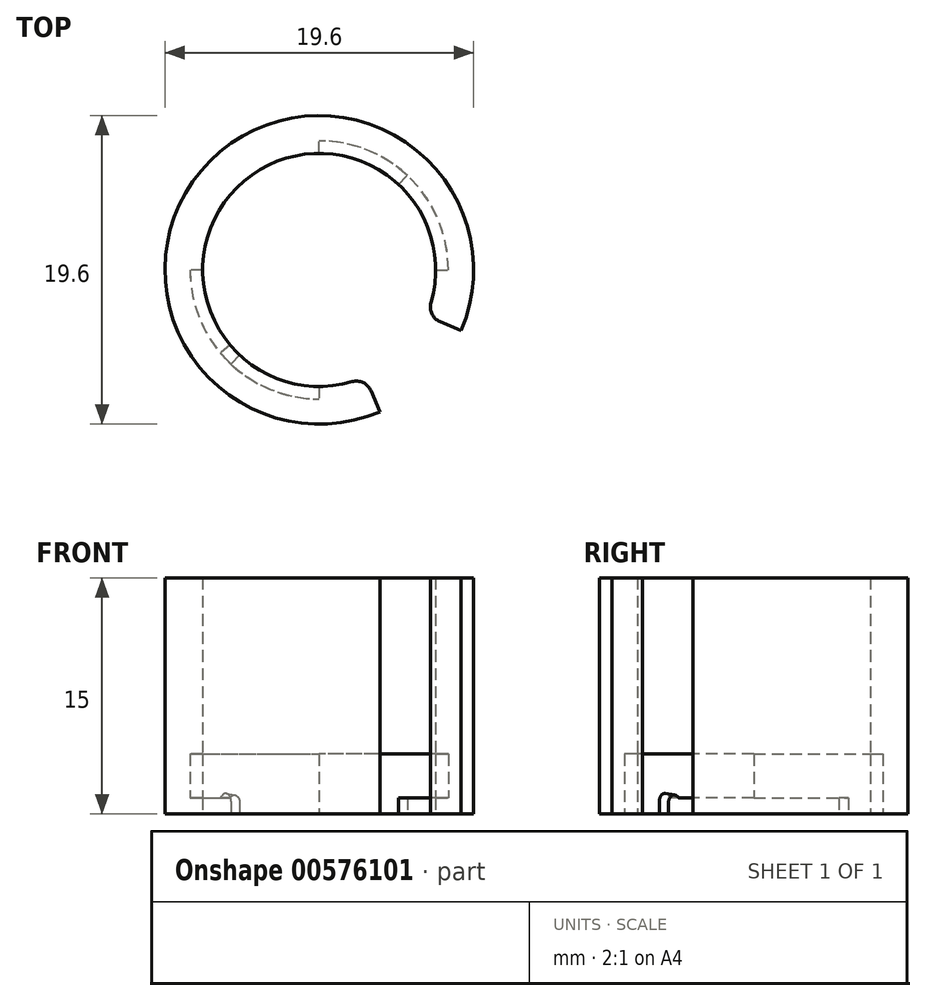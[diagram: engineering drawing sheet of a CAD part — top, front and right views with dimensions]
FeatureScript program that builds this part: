
annotation { "Feature Type Name" : "Feature", "Feature Type Description" : "" }
export const myFeature = defineFeature(function(context is Context, id is Id, definition is map)
    precondition{}
    {
        {
            var Q0;
            Q0=qCreatedBy(makeId("Top.planeOp"),FACE);
            var sketch = newSketch(context, id + "F0", { "sketchPlane" : qUnion([Q0])});
            skCircle(sketch, "E0", {"center": v(0, 0) * mm, "radius": 7.4 * mm});
            skCircle(sketch, "E1", {"center": v(0, 0) * mm, "radius": 9.8 * mm});
            skSolve(sketch);
        }
        {
            var Q0;
            Q0 = qSketchRegion(id + "F0", true);
            extrude(context, id + "F1", {"entities" : qUnion([Q0]), "depth" : 10 * mm, "offsetDistance" : 25 * mm});
        }
        {
            var Q0;
            Q0=qCreatedBy(makeId("Top.planeOp"),FACE);
            cPlane(context, id + "F2", {"entities" : qUnion([Q0]), "cplaneType" : CPlaneType.OFFSET, "offset" : 1 * mm, "width" : 150 * mm, "height" : 150 * mm});
        }
        {
            var Q0;
            Q0=qCreatedBy(id+"F2.planeOp",FACE);
            var sketch = newSketch(context, id + "F3", { "sketchPlane" : qUnion([Q0])});
            skCircle(sketch, "E2.0", {"center": v(0, 0) * mm, "radius": 7.4 * mm});
            skArc(sketch, "E3", {"start": v(-8.2, 0) * mm, "mid": v(-5.8, -5.8) * mm, "end": v(0, -8.2) * mm});
            skLineSegment(sketch, "E4", {"start": v(0, 0) * mm, "end": v(-8.2, 0) * mm});
            skLineSegment(sketch, "E5", {"start": v(0, 0) * mm, "end": v(0, -8.2) * mm});
            skLineSegment(sketch, "E6", {"start": v(0, 0) * mm, "end": v(0, 8.2) * mm});
            skLineSegment(sketch, "E7", {"start": v(0, 0) * mm, "end": v(8.2, 0) * mm});
            skArc(sketch, "E8.trimOffspring", {"start": v(8.2, 0) * mm, "mid": v(5.8, 5.8) * mm, "end": v(0, 8.2) * mm});
            skSolve(sketch);
        }
        {
            var Q0;
            {var subQ5=sQuery(id+"F3.wireOp",EDGE,"E8.trimOffspring");Q0=makeQuery(id+"F3.imprint","IMPRINT",FACE,{"disambiguationData":[TD([[makeQuery(id+"F3.imprint","IMPRINT",EDGE,{"derivedFrom":subQ5}),1.0]])]});}
            var Q1;
            {var subQ5=sQuery(id+"F3.wireOp",EDGE,"E3");Q1=makeQuery(id+"F3.imprint","IMPRINT",FACE,{"disambiguationData":[TD([[makeQuery(id+"F3.imprint","IMPRINT",EDGE,{"derivedFrom":subQ5}),1.0]])]});}
            extrude(context, id + "F4", {"entities" : qUnion([Q0, Q1]), "operationType" : NewBodyOperationType.REMOVE, "depth" : 2.8 * mm, "offsetDistance" : 25 * mm});
        }
        {
            var Q0;
            Q0=makeQuery(id+"F4.boolean.opBoolean","COPY",FACE,{"derivedFrom":makeQuery(id+"F4.opExtrude","CAP_FACE",FACE,{"disambiguationData":[OSD([sQuery(id+"F3.wireOp",EDGE,"E2.0"),sQuery(id+"F3.wireOp",EDGE,"E3"),sQuery(id+"F3.wireOp",EDGE,"E4"),sQuery(id+"F3.wireOp",EDGE,"E5")])],"isStart":true})});
            var sketch = newSketch(context, id + "F5", { "sketchPlane" : qUnion([Q0])});
            skArc(sketch, "E9.0.0", {"start": v(0, -7.4) * mm, "mid": v(-5.23, -5.23) * mm, "end": v(-7.4, 0) * mm});
            skLineSegment(sketch, "E9.0.1", {"start": v(-7.4, 0) * mm, "end": v(-8.2, 0) * mm});
            skArc(sketch, "E9.0.2", {"start": v(-8.2, 0) * mm, "mid": v(-5.8, -5.8) * mm, "end": v(0, -8.2) * mm});
            skLineSegment(sketch, "E9.0.3", {"start": v(0, -8.2) * mm, "end": v(0, -7.4) * mm});
            skArc(sketch, "E10.0.0", {"start": v(0, 7.4) * mm, "mid": v(5.23, 5.23) * mm, "end": v(7.4, 0) * mm});
            skLineSegment(sketch, "E10.0.1", {"start": v(7.4, 0) * mm, "end": v(8.2, 0) * mm});
            skArc(sketch, "E10.0.2", {"start": v(8.2, 0) * mm, "mid": v(5.8, 5.8) * mm, "end": v(0, 8.2) * mm});
            skLineSegment(sketch, "E10.0.3", {"start": v(0, 8.2) * mm, "end": v(0, 7.4) * mm});
            skLineSegment(sketch, "E11", {"start": v(0, 0) * mm, "end": v(5.05, 6.46) * mm});
            skLineSegment(sketch, "E12", {"start": v(0, 0) * mm, "end": v(-5.05, -6.46) * mm});
            skLineSegment(sketch, "E13", {"start": v(0, 0) * mm, "end": v(-6.28, -5.27) * mm});
            skLineSegment(sketch, "E14", {"start": v(0, 0) * mm, "end": v(6.28, 5.27) * mm});
            skSolve(sketch);
        }
        {
            var Q0;
            {var subQ0=sQuery(id+"F5.wireOp",EDGE,"E13");var subQ1=sQuery(id+"F5.wireOp",EDGE,"E9.0.0");var subQ2=makeQuery(id+"F5.imprint","INTERSECT",VERTEX,{"derivedFrom":[subQ1,subQ0]});Q0=makeQuery(id+"F5.imprint","IMPRINT",FACE,{"disambiguationData":[TD([[makeQuery(id+"F5.imprint","IMPRINT",EDGE,{"disambiguationData":[TD([[subQ2,-1.0]])],"derivedFrom":subQ1}),-1.0]])]});}
            var Q1;
            {var subQ0=sQuery(id+"F5.wireOp",EDGE,"E11");var subQ1=sQuery(id+"F5.wireOp",EDGE,"E10.0.0");var subQ2=makeQuery(id+"F5.imprint","INTERSECT",VERTEX,{"derivedFrom":[subQ1,subQ0]});Q1=makeQuery(id+"F5.imprint","IMPRINT",FACE,{"disambiguationData":[TD([[makeQuery(id+"F5.imprint","IMPRINT",EDGE,{"disambiguationData":[TD([[subQ2,-1.0]])],"derivedFrom":subQ1}),1.0]])]});}
            extrude(context, id + "F6", {"entities" : qUnion([Q0, Q1]), "operationType" : NewBodyOperationType.ADD, "depth" : 1 * mm, "offsetDistance" : 25 * mm});
        }
        {
            var Q0;
            Q0=makeQuery(id+"F6.opExtrude","CAP_EDGE",EDGE,{"disambiguationData":[OSD([sQuery(id+"F5.wireOp",EDGE,"E14")])],"isStart":false});
            var Q1;
            Q1=makeQuery(id+"F6.opExtrude","CAP_EDGE",EDGE,{"disambiguationData":[OSD([sQuery(id+"F5.wireOp",EDGE,"E13")])],"isStart":false});
            chamfer(context, id + "F7", {"entities" : qUnion([Q0, Q1]), "width" : 1 * mm, "tangentPropagation" : true});
        }
        {
            var Q0;
            Q0=makeQuery(id+"F6.opExtrude","CAP_EDGE",EDGE,{"disambiguationData":[OSD([sQuery(id+"F5.wireOp",EDGE,"E12")])],"isStart":false});
            var Q1;
            Q1=makeQuery(id+"F6.opExtrude","CAP_EDGE",EDGE,{"disambiguationData":[OSD([sQuery(id+"F5.wireOp",EDGE,"E11")])],"isStart":false});
            fillet(context, id + "F8", {"entities" : qUnion([Q0, Q1]), "radius" : 0.5 * mm, "tangentPropagation" : true, "allowEdgeOverflow" : false});
        }
        {
            var Q0;
            Q0=makeQuery(id+"F1.opExtrude","CAP_FACE",FACE,{"disambiguationData":[OSD([sQuery(id+"F0.wireOp",EDGE,"E0"),sQuery(id+"F0.wireOp",EDGE,"E1")])],"isStart":true});
            var sketch = newSketch(context, id + "F9", { "sketchPlane" : qUnion([Q0])});
            skArc(sketch, "E15.0.0", {"start": v(7.4, 0) * mm, "mid": v(5.23, -5.23) * mm, "end": v(0, -7.4) * mm});
            skLineSegment(sketch, "E15.0.1", {"start": v(0, -7.4) * mm, "end": v(0, -8.2) * mm});
            skArc(sketch, "E15.0.2", {"start": v(0, -8.2) * mm, "mid": v(5.8, -5.8) * mm, "end": v(8.2, 0) * mm});
            skLineSegment(sketch, "E15.0.3", {"start": v(8.2, 0) * mm, "end": v(7.4, 0) * mm});
            skArc(sketch, "E16.0.0", {"start": v(-7.4, 0) * mm, "mid": v(-5.23, 5.23) * mm, "end": v(0, 7.4) * mm});
            skLineSegment(sketch, "E16.0.1", {"start": v(0, 7.4) * mm, "end": v(0, 8.2) * mm});
            skArc(sketch, "E16.0.2", {"start": v(0, 8.2) * mm, "mid": v(-5.8, 5.8) * mm, "end": v(-8.2, 0) * mm});
            skLineSegment(sketch, "E16.0.3", {"start": v(-8.2, 0) * mm, "end": v(-7.4, 0) * mm});
            skLineSegment(sketch, "E17", {"start": v(-5.05, 5.41) * mm, "end": v(-5.6, 6) * mm});
            skLineSegment(sketch, "E18", {"start": v(5.05, -5.41) * mm, "end": v(5.6, -6) * mm});
            skSolve(sketch);
        }
        {
            var Q0;
            {var subQ0=sQuery(id+"F9.wireOp",EDGE,"E15.0.1");Q0=makeQuery(id+"F9.imprint","IMPRINT",FACE,{"disambiguationData":[TD([[makeQuery(id+"F9.imprint","IMPRINT",EDGE,{"derivedFrom":subQ0}),1.0]])]});}
            var Q1;
            {var subQ0=sQuery(id+"F9.wireOp",EDGE,"E16.0.1");Q1=makeQuery(id+"F9.imprint","IMPRINT",FACE,{"disambiguationData":[TD([[makeQuery(id+"F9.imprint","IMPRINT",EDGE,{"derivedFrom":subQ0}),1.0]])]});}
            var Q2;
            {var subQ0=sQuery(id+"F3.wireOp",EDGE,"E8.trimOffspring");var subQ1=sQuery(id+"F3.wireOp",EDGE,"E6");Q2=makeQuery(id+"F6.boolean.opBoolean","SPLIT",FACE,{"disambiguationData":[TD([makeQuery(id+"F4.boolean.opBoolean","COPY",FACE,{"derivedFrom":makeQuery(id+"F4.opExtrude","SWEPT_FACE",FACE,{"disambiguationData":[OSD([subQ1])]})})])],"derivedFrom":makeQuery(id+"F4.boolean.opBoolean","COPY",FACE,{"derivedFrom":makeQuery(id+"F4.opExtrude","CAP_FACE",FACE,{"disambiguationData":[OSD([sQuery(id+"F3.wireOp",EDGE,"E2.0"),subQ1,sQuery(id+"F3.wireOp",EDGE,"E7"),subQ0])],"isStart":true})})});}
            extrude(context, id + "F10", {"entities" : qUnion([Q0, Q1]), "operationType" : NewBodyOperationType.REMOVE, "oppositeDirection" : true, "depth" : 3 * mm, "endBoundEntityFace" : qUnion([Q2]), "offsetDistance" : 25 * mm});
        }
        {
            var Q0;
            Q0=makeQuery(id+"F10.boolean.opBoolean","INTERSECT",EDGE,{"derivedFrom":[makeQuery(id+"F7.opChamfer","BLEND_FACE",FACE,{"disambiguationData":[OSD([sQuery(id+"F5.wireOp",EDGE,"E14")])]}),makeQuery(id+"F10.opExtrude","SWEPT_FACE",FACE,{"disambiguationData":[OSD([sQuery(id+"F9.wireOp",EDGE,"E18")])]})]});
            var Q1;
            Q1=makeQuery(id+"F10.boolean.opBoolean","INTERSECT",EDGE,{"derivedFrom":[makeQuery(id+"F7.opChamfer","BLEND_FACE",FACE,{"disambiguationData":[OSD([sQuery(id+"F5.wireOp",EDGE,"E13")])]}),makeQuery(id+"F10.opExtrude","SWEPT_FACE",FACE,{"disambiguationData":[OSD([sQuery(id+"F9.wireOp",EDGE,"E17")])]})]});
            fillet(context, id + "F11", {"entities" : qUnion([Q0, Q1]), "radius" : 0.5 * mm, "tangentPropagation" : true, "allowEdgeOverflow" : false});
        }
        {
            var Q0;
            Q0=makeQuery(id+"F1.opExtrude","CAP_FACE",FACE,{"disambiguationData":[OSD([sQuery(id+"F0.wireOp",EDGE,"E0"),sQuery(id+"F0.wireOp",EDGE,"E1")])],"isStart":true});
            var sketch = newSketch(context, id + "F12", { "sketchPlane" : qUnion([Q0])});
            skCircle(sketch, "E19.0.0", {"center": v(0, 0) * mm, "radius": 9.8 * mm});
            skSolve(sketch);
        }
        {
            var Q0;
            Q0=makeQuery(id+"F1.opExtrude","CAP_FACE",FACE,{"disambiguationData":[OSD([sQuery(id+"F0.wireOp",EDGE,"E0"),sQuery(id+"F0.wireOp",EDGE,"E1")])],"isStart":false});
            extrude(context, id + "F13", {"entities" : qUnion([Q0]), "operationType" : NewBodyOperationType.ADD, "depth" : 5 * mm, "offsetDistance" : 25 * mm});
        }
        {
            var Q0;
            Q0=makeQuery(id+"F13.opExtrude","CAP_FACE",FACE,{"disambiguationData":[OSD([sQuery(id+"F0.wireOp",EDGE,"E0"),sQuery(id+"F0.wireOp",EDGE,"E1")])],"isStart":false});
            var sketch = newSketch(context, id + "F14", { "sketchPlane" : qUnion([Q0])});
            skCircle(sketch, "E20.0.0", {"center": v(0, 0) * mm, "radius": 9.8 * mm});
            skCircle(sketch, "E21.0", {"center": v(0, 0) * mm, "radius": 7.4 * mm});
            skLineSegment(sketch, "E22", {"start": v(0, 0) * mm, "end": v(8.18, -8.18) * mm, "construction": true});
            skLineSegment(sketch, "E23", {"start": v(0, 0) * mm, "end": v(4.47, -10.43) * mm});
            skLineSegment(sketch, "E24", {"start": v(0, 0) * mm, "end": v(9.6, -4.12) * mm});
            skLineSegment(sketch, "E25", {"start": v(6.8, -2.91) * mm, "end": v(2.91, -6.8) * mm, "construction": true});
            skArc(sketch, "E26", {"start": v(4.47, -10.43) * mm, "mid": v(8.29, -8.29) * mm, "end": v(9.6, -4.12) * mm});
            skSolve(sketch);
        }
        {
            var Q0;
            {var subQ5=sQuery(id+"F14.wireOp",EDGE,"E26");Q0=makeQuery(id+"F14.imprint","IMPRINT",FACE,{"disambiguationData":[TD([[makeQuery(id+"F14.imprint","IMPRINT",EDGE,{"derivedFrom":subQ5}),1.0]])]});}
            var Q1;
            {var subQ0=sQuery(id+"F14.wireOp",EDGE,"E23");var subQ1=sQuery(id+"F14.wireOp",EDGE,"E20.0.0");var subQ2=makeQuery(id+"F14.imprint","INTERSECT",VERTEX,{"derivedFrom":[subQ1,subQ0]});Q1=makeQuery(id+"F14.imprint","IMPRINT",FACE,{"disambiguationData":[TD([[makeQuery(id+"F14.imprint","IMPRINT",EDGE,{"disambiguationData":[TD([[subQ2,-1.0]])],"derivedFrom":subQ1}),1.0]])]});}
            var Q2;
            {var subQ0=sQuery(id+"F14.wireOp",EDGE,"E23");var subQ1=sQuery(id+"F14.wireOp",EDGE,"E21.0");var subQ2=makeQuery(id+"F14.imprint","INTERSECT",VERTEX,{"derivedFrom":[subQ1,subQ0]});Q2=makeQuery(id+"F14.imprint","IMPRINT",FACE,{"disambiguationData":[TD([[makeQuery(id+"F14.imprint","IMPRINT",EDGE,{"disambiguationData":[TD([[subQ2,-1.0]])],"derivedFrom":subQ1}),1.0]])]});}
            extrude(context, id + "F15", {"entities" : qUnion([Q0, Q1, Q2]), "operationType" : NewBodyOperationType.REMOVE, "oppositeDirection" : true, "depth" : 25 * mm, "offsetDistance" : 25 * mm});
        }
        {
            var Q0;
            {var subQ0=sQuery(id+"F0.wireOp",EDGE,"E0");Q0=makeQuery(id+"F15.boolean.opBoolean","INTERSECT",EDGE,{"derivedFrom":[makeQuery(id+"F13.boolean.opBoolean","MERGE",FACE,{"derivedFrom":[makeQuery(id+"F6.boolean.opBoolean","MERGE",FACE,{"derivedFrom":[makeQuery(id+"F1.opExtrude","SWEPT_FACE",FACE,{"disambiguationData":[OSD([subQ0])]}),makeQuery(id+"F6.opExtrude","SWEPT_FACE",FACE,{"disambiguationData":[OSD([sQuery(id+"F5.wireOp",EDGE,"E9.0.0")])]}),makeQuery(id+"F6.opExtrude","SWEPT_FACE",FACE,{"disambiguationData":[OSD([sQuery(id+"F5.wireOp",EDGE,"E10.0.0")])]})]}),makeQuery(id+"F13.opExtrude","SWEPT_FACE",FACE,{"disambiguationData":[OSD([subQ0])]})]}),makeQuery(id+"F15.opExtrude","SWEPT_FACE",FACE,{"disambiguationData":[OSD([sQuery(id+"F14.wireOp",EDGE,"E23")])]})]});}
            var Q1;
            {var subQ0=sQuery(id+"F0.wireOp",EDGE,"E0");Q1=makeQuery(id+"F15.boolean.opBoolean","INTERSECT",EDGE,{"derivedFrom":[makeQuery(id+"F13.boolean.opBoolean","MERGE",FACE,{"derivedFrom":[makeQuery(id+"F6.boolean.opBoolean","MERGE",FACE,{"derivedFrom":[makeQuery(id+"F1.opExtrude","SWEPT_FACE",FACE,{"disambiguationData":[OSD([subQ0])]}),makeQuery(id+"F6.opExtrude","SWEPT_FACE",FACE,{"disambiguationData":[OSD([sQuery(id+"F5.wireOp",EDGE,"E9.0.0")])]}),makeQuery(id+"F6.opExtrude","SWEPT_FACE",FACE,{"disambiguationData":[OSD([sQuery(id+"F5.wireOp",EDGE,"E10.0.0")])]})]}),makeQuery(id+"F13.opExtrude","SWEPT_FACE",FACE,{"disambiguationData":[OSD([subQ0])]})]}),makeQuery(id+"F15.opExtrude","SWEPT_FACE",FACE,{"disambiguationData":[OSD([sQuery(id+"F14.wireOp",EDGE,"E24")])]})]});}
            fillet(context, id + "F16", {"entities" : qUnion([Q0, Q1]), "radius" : 1 * mm, "tangentPropagation" : true, "allowEdgeOverflow" : false});
        }
    });
